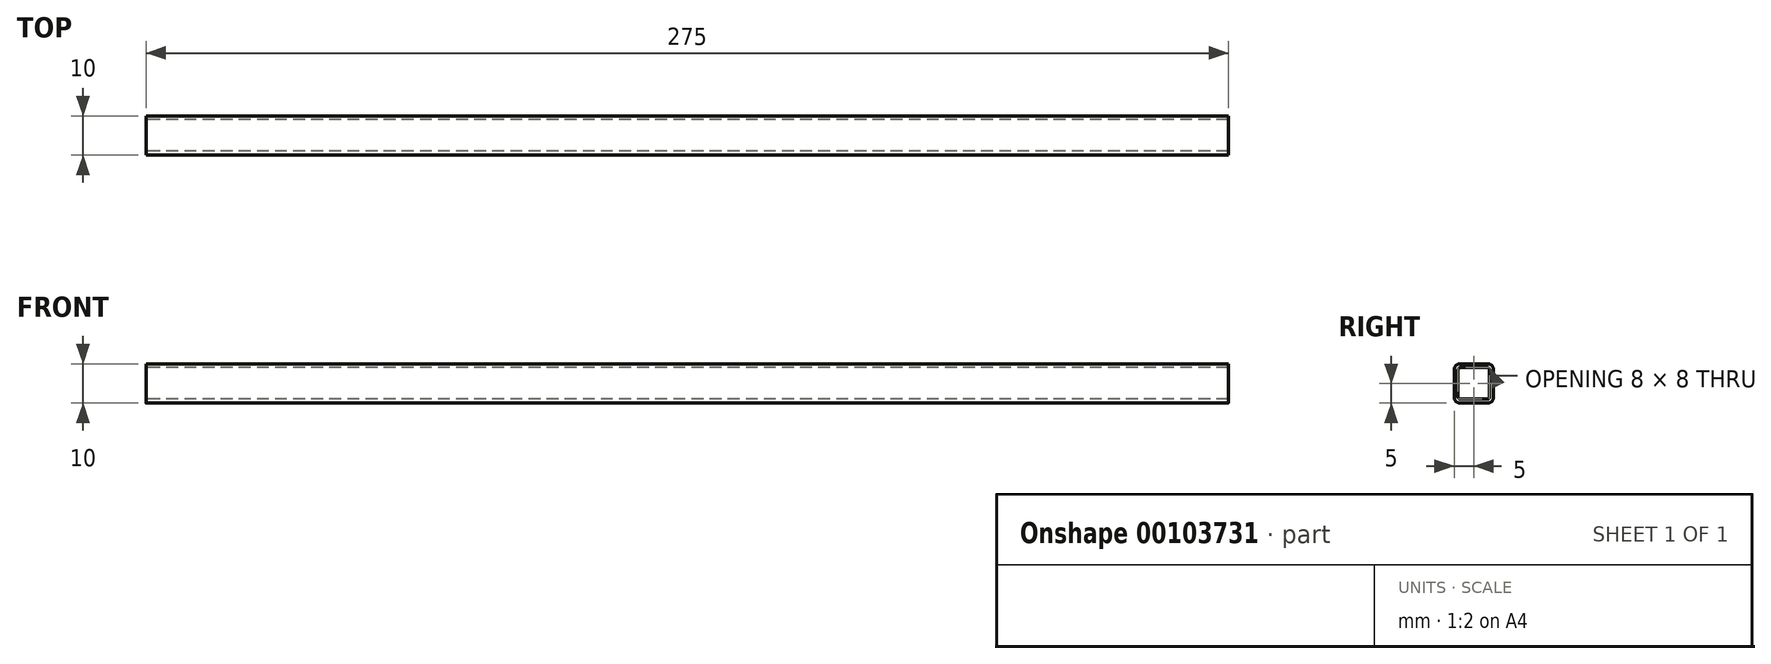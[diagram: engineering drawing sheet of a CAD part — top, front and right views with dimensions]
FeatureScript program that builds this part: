
annotation { "Feature Type Name" : "Feature", "Feature Type Description" : "" }
export const myFeature = defineFeature(function(context is Context, id is Id, definition is map)
    precondition{}
    {
        {
            var Q0;
            Q0=qCreatedBy(makeId("Right.planeOp"),FACE);
            var sketch = newSketch(context, id + "F0", { "sketchPlane" : qUnion([Q0])});
            skLineSegment(sketch, "E0.bottom", {"start": v(-3.5, -4) * mm, "end": v(3.5, -4) * mm});
            skLineSegment(sketch, "E0.top", {"start": v(-3.5, 4) * mm, "end": v(3.5, 4) * mm});
            skLineSegment(sketch, "E0.left", {"start": v(-4, -3.5) * mm, "end": v(-4, 3.5) * mm});
            skLineSegment(sketch, "E0.right", {"start": v(4, -3.5) * mm, "end": v(4, 3.5) * mm});
            skPoint(sketch, "E0.middle", {"position": v(0, 0) * mm});
            skPoint(sketch, "E1.visualSharp", {"position": v(4, 4) * mm});
            skArc(sketch, "E1.filletArc", {"start": v(4, 3.5) * mm, "mid": v(3.85, 3.85) * mm, "end": v(3.5, 4) * mm});
            skPoint(sketch, "E2.visualSharp", {"position": v(-4, 4) * mm});
            skArc(sketch, "E2.filletArc", {"start": v(-3.5, 4) * mm, "mid": v(-3.85, 3.85) * mm, "end": v(-4, 3.5) * mm});
            skPoint(sketch, "E3.visualSharp", {"position": v(-4, -4) * mm});
            skArc(sketch, "E3.filletArc", {"start": v(-4, -3.5) * mm, "mid": v(-3.85, -3.85) * mm, "end": v(-3.5, -4) * mm});
            skPoint(sketch, "E4.visualSharp", {"position": v(4, -4) * mm});
            skArc(sketch, "E4.filletArc", {"start": v(3.5, -4) * mm, "mid": v(3.85, -3.85) * mm, "end": v(4, -3.5) * mm});
            skArc(sketch, "E5.0", {"start": v(3.5, -5) * mm, "mid": v(4.56, -4.56) * mm, "end": v(5, -3.5) * mm});
            skLineSegment(sketch, "E5.1", {"start": v(-3.5, -5) * mm, "end": v(3.5, -5) * mm});
            skLineSegment(sketch, "E5.2", {"start": v(5, -3.5) * mm, "end": v(5, 3.5) * mm});
            skArc(sketch, "E5.3", {"start": v(-5, -3.5) * mm, "mid": v(-4.56, -4.56) * mm, "end": v(-3.5, -5) * mm});
            skArc(sketch, "E5.4", {"start": v(5, 3.5) * mm, "mid": v(4.56, 4.56) * mm, "end": v(3.5, 5) * mm});
            skLineSegment(sketch, "E5.5", {"start": v(-3.5, 5) * mm, "end": v(3.5, 5) * mm});
            skArc(sketch, "E5.6", {"start": v(-3.5, 5) * mm, "mid": v(-4.56, 4.56) * mm, "end": v(-5, 3.5) * mm});
            skLineSegment(sketch, "E5.7", {"start": v(-5, -3.5) * mm, "end": v(-5, 3.5) * mm});
            skSolve(sketch);
        }
        {
            var Q0;
            Q0=qSketchRegion(id+"F0",true);
            extrude(context, id + "F1", {"entities" : qUnion([Q0]), "endBound" : BoundingType.SYMMETRIC, "depth" : 275 * mm});
        }
    });
